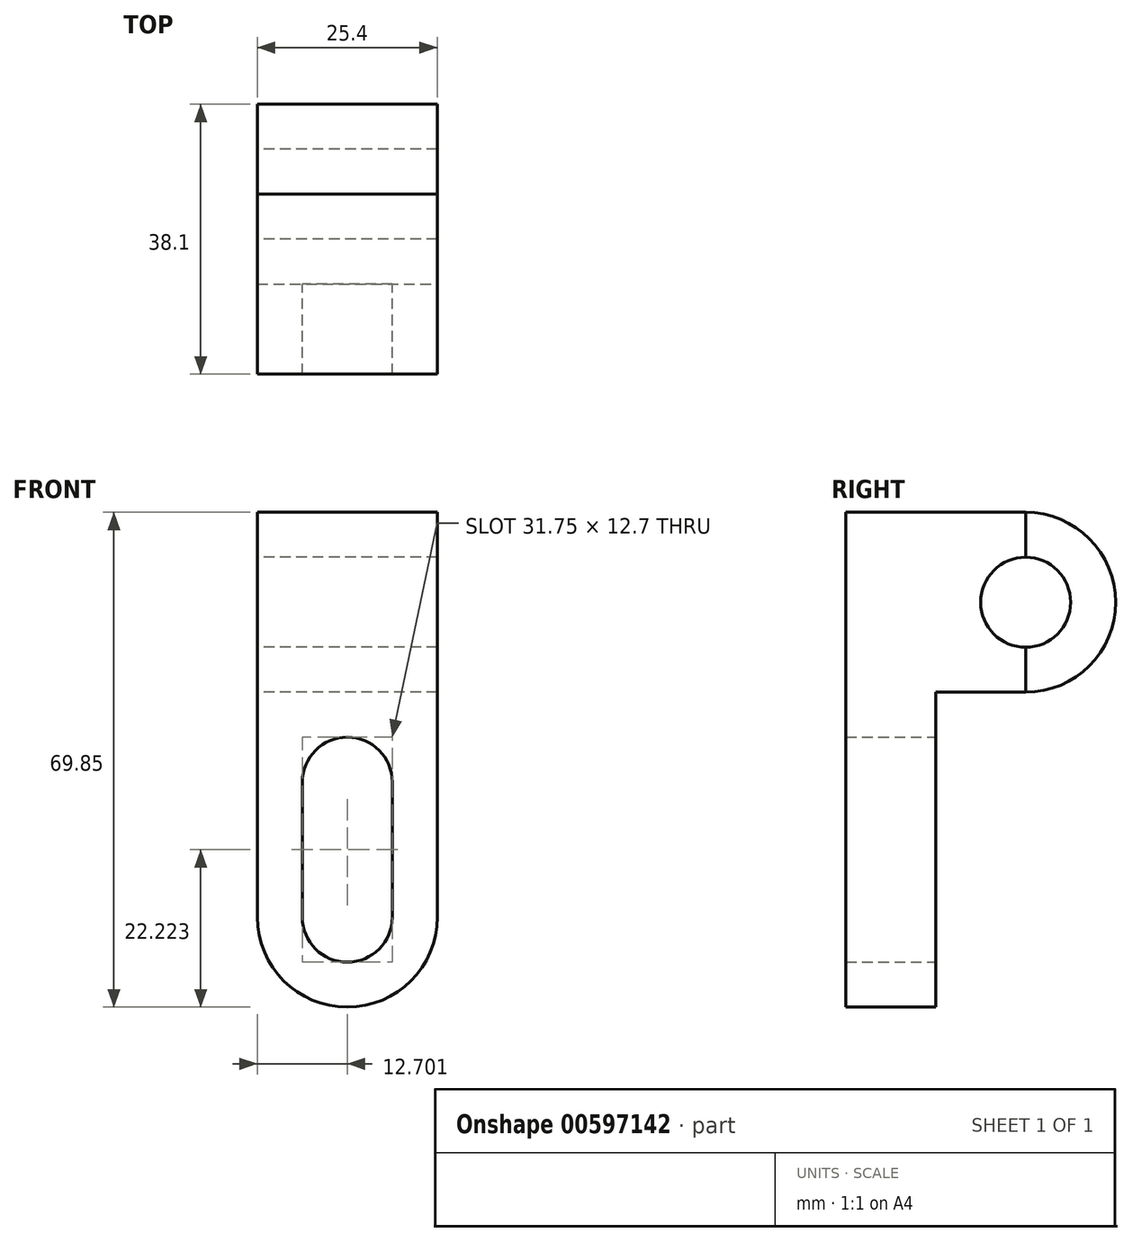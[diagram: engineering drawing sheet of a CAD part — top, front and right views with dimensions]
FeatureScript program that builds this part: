
annotation { "Feature Type Name" : "Feature", "Feature Type Description" : "" }
export const myFeature = defineFeature(function(context is Context, id is Id, definition is map)
    precondition{}
    {
        {
            var Q0;
            Q0=qCreatedBy(makeId("Front.planeOp"),FACE);
            var sketch = newSketch(context, id + "F0", { "sketchPlane" : qUnion([Q0])});
            skLineSegment(sketch, "E0", {"start": v(-59.54, 62.27) * mm, "end": v(-59.54, 5.12) * mm});
            skLineSegment(sketch, "E1", {"start": v(-59.54, 5.12) * mm, "end": v(-34.14, 5.12) * mm});
            skLineSegment(sketch, "E2", {"start": v(-34.14, 5.12) * mm, "end": v(-34.14, 62.27) * mm});
            skLineSegment(sketch, "E3", {"start": v(-34.14, 62.27) * mm, "end": v(-59.54, 62.27) * mm});
            skSolve(sketch);
        }
        {
            var Q0;
            Q0=makeQuery(id+"F0.imprint","IMPRINT",FACE,{"disambiguationData":[TD([[makeQuery(id+"F0.imprint","IMPRINT",EDGE,{"derivedFrom":sQuery(id+"F0.wireOp",EDGE,"E0")}),1.0]])]});
            extrude(context, id + "F1", {"entities" : qUnion([Q0]), "depth" : 12.7 * mm, "offsetDistance" : 25.4 * mm});
        }
        {
            var Q0;
            Q0=makeQuery(id+"F1.opExtrude","CAP_FACE",FACE,{"disambiguationData":[OSD([sQuery(id+"F0.wireOp",EDGE,"E0"),sQuery(id+"F0.wireOp",EDGE,"E1"),sQuery(id+"F0.wireOp",EDGE,"E2"),sQuery(id+"F0.wireOp",EDGE,"E3")])],"isStart":false});
            var sketch = newSketch(context, id + "F2", { "sketchPlane" : qUnion([Q0])});
            skArc(sketch, "E4", {"start": v(-59.54, 5.12) * mm, "mid": v(-46.84, -7.58) * mm, "end": v(-34.14, 5.12) * mm});
            skSolve(sketch);
        }
        {
            var Q0;
            Q0=makeQuery(id+"F2.imprint","IMPRINT",FACE,{"disambiguationData":[TD([[makeQuery(id+"F2.imprint","IMPRINT",EDGE,{"derivedFrom":sQuery(id+"F2.wireOp",EDGE,"E4")}),1.0]])]});
            var sketch = newSketch(context, id + "F3", { "sketchPlane" : qUnion([Q0])});
            skSolve(sketch);
        }
        {
            var Q0;
            Q0 = qSketchRegion(id + "F3", true);
            var Q1;
            Q1=makeQuery(id+"F2.imprint","IMPRINT",FACE,{"disambiguationData":[TD([[makeQuery(id+"F2.imprint","IMPRINT",EDGE,{"derivedFrom":sQuery(id+"F2.wireOp",EDGE,"E4")}),1.0]])]});
            extrude(context, id + "F4", {"entities" : qUnion([Q0, Q1]), "operationType" : NewBodyOperationType.ADD, "oppositeDirection" : true, "depth" : 12.7 * mm, "offsetDistance" : 25.4 * mm});
        }
        {
            var Q0;
            {var subQ0=sQuery(id+"F0.wireOp",EDGE,"E1");Q0=makeQuery(id+"F4.boolean.opBoolean","MERGE",FACE,{"derivedFrom":[makeQuery(id+"F1.opExtrude","CAP_FACE",FACE,{"disambiguationData":[OSD([sQuery(id+"F0.wireOp",EDGE,"E0"),subQ0,sQuery(id+"F0.wireOp",EDGE,"E2"),sQuery(id+"F0.wireOp",EDGE,"E3")])],"isStart":true}),makeQuery(id+"F4.opExtrude","CAP_FACE",FACE,{"disambiguationData":[OSD([subQ0,sQuery(id+"F2.wireOp",EDGE,"E4")])],"isStart":false})]});}
            var sketch = newSketch(context, id + "F5", { "sketchPlane" : qUnion([Q0])});
            skLineSegment(sketch, "E5", {"start": v(34.14, 62.27) * mm, "end": v(34.14, 36.87) * mm});
            skLineSegment(sketch, "E6", {"start": v(34.14, 36.87) * mm, "end": v(59.54, 36.87) * mm});
            skLineSegment(sketch, "E7", {"start": v(59.54, 36.87) * mm, "end": v(59.54, 62.27) * mm});
            skLineSegment(sketch, "E8", {"start": v(59.54, 62.27) * mm, "end": v(34.14, 62.27) * mm});
            skLineSegment(sketch, "E9", {"start": v(40.49, 24.17) * mm, "end": v(40.49, 5.12) * mm});
            skLineSegment(sketch, "E10", {"start": v(40.49, 5.12) * mm, "end": v(53.19, 5.12) * mm});
            skLineSegment(sketch, "E11", {"start": v(53.19, 5.12) * mm, "end": v(53.19, 24.17) * mm});
            skLineSegment(sketch, "E12", {"start": v(53.19, 24.17) * mm, "end": v(40.49, 24.17) * mm});
            skSolve(sketch);
        }
        {
            var Q0;
            Q0=makeQuery(id+"F5.imprint","IMPRINT",FACE,{"disambiguationData":[TD([[makeQuery(id+"F5.imprint","IMPRINT",EDGE,{"derivedFrom":sQuery(id+"F5.wireOp",EDGE,"E9")}),1.0]])]});
            extrude(context, id + "F6", {"entities" : qUnion([Q0]), "operationType" : NewBodyOperationType.REMOVE, "oppositeDirection" : true, "depth" : 25.4 * mm, "offsetDistance" : 25.4 * mm});
        }
        {
            var Q0;
            {var subQ0=sQuery(id+"F0.wireOp",EDGE,"E1");Q0=makeQuery(id+"F4.boolean.opBoolean","MERGE",FACE,{"derivedFrom":[makeQuery(id+"F1.opExtrude","CAP_FACE",FACE,{"disambiguationData":[OSD([sQuery(id+"F0.wireOp",EDGE,"E0"),subQ0,sQuery(id+"F0.wireOp",EDGE,"E2"),sQuery(id+"F0.wireOp",EDGE,"E3")])],"isStart":true}),makeQuery(id+"F4.opExtrude","CAP_FACE",FACE,{"disambiguationData":[OSD([subQ0,sQuery(id+"F2.wireOp",EDGE,"E4")])],"isStart":false})]});}
            var sketch = newSketch(context, id + "F7", { "sketchPlane" : qUnion([Q0])});
            skArc(sketch, "E13", {"start": v(53.19, 24.17) * mm, "mid": v(46.84, 30.52) * mm, "end": v(40.49, 24.17) * mm});
            skArc(sketch, "E14", {"start": v(40.49, 5.12) * mm, "mid": v(46.84, -1.23) * mm, "end": v(53.19, 5.12) * mm});
            skSolve(sketch);
        }
        {
            var Q0;
            Q0 = qSketchRegion(id + "F7", true);
            var Q1;
            Q1=makeQuery(id+"F7.imprint","IMPRINT",FACE,{"disambiguationData":[TD([[makeQuery(id+"F7.imprint","IMPRINT",EDGE,{"derivedFrom":sQuery(id+"F7.wireOp",EDGE,"E13")}),1.0]])]});
            extrude(context, id + "F8", {"entities" : qUnion([Q0, Q1]), "operationType" : NewBodyOperationType.REMOVE, "oppositeDirection" : true, "depth" : 25.4 * mm, "offsetDistance" : 25.4 * mm});
        }
        {
            var Q0;
            {var subQ0=sQuery(id+"F0.wireOp",EDGE,"E1");Q0=makeQuery(id+"F4.boolean.opBoolean","MERGE",FACE,{"derivedFrom":[makeQuery(id+"F1.opExtrude","CAP_FACE",FACE,{"disambiguationData":[OSD([sQuery(id+"F0.wireOp",EDGE,"E0"),subQ0,sQuery(id+"F0.wireOp",EDGE,"E2"),sQuery(id+"F0.wireOp",EDGE,"E3")])],"isStart":true}),makeQuery(id+"F4.opExtrude","CAP_FACE",FACE,{"disambiguationData":[OSD([subQ0,sQuery(id+"F2.wireOp",EDGE,"E4")])],"isStart":false})]});}
            var sketch = newSketch(context, id + "F9", { "sketchPlane" : qUnion([Q0])});
            skArc(sketch, "E15", {"start": v(40.49, 5.12) * mm, "mid": v(46.84, -1.23) * mm, "end": v(53.19, 5.12) * mm});
            skSolve(sketch);
        }
        {
            var Q0;
            Q0 = qSketchRegion(id + "F9", true);
            var Q1;
            Q1=makeQuery(id+"F9.imprint","IMPRINT",FACE,{"disambiguationData":[TD([[makeQuery(id+"F9.imprint","IMPRINT",EDGE,{"derivedFrom":sQuery(id+"F9.wireOp",EDGE,"E15")}),1.0]])]});
            extrude(context, id + "F10", {"entities" : qUnion([Q0, Q1]), "operationType" : NewBodyOperationType.REMOVE, "oppositeDirection" : true, "depth" : 25.4 * mm, "offsetDistance" : 25.4 * mm});
        }
        {
            var Q0;
            {var subQ0=sQuery(id+"F0.wireOp",EDGE,"E1");Q0=makeQuery(id+"F4.boolean.opBoolean","MERGE",FACE,{"derivedFrom":[makeQuery(id+"F1.opExtrude","CAP_FACE",FACE,{"disambiguationData":[OSD([sQuery(id+"F0.wireOp",EDGE,"E0"),subQ0,sQuery(id+"F0.wireOp",EDGE,"E2"),sQuery(id+"F0.wireOp",EDGE,"E3")])],"isStart":true}),makeQuery(id+"F4.opExtrude","CAP_FACE",FACE,{"disambiguationData":[OSD([subQ0,sQuery(id+"F2.wireOp",EDGE,"E4")])],"isStart":false})]});}
            var sketch = newSketch(context, id + "F11", { "sketchPlane" : qUnion([Q0])});
            skLineSegment(sketch, "E16", {"start": v(34.14, 62.27) * mm, "end": v(34.14, 36.87) * mm});
            skLineSegment(sketch, "E17", {"start": v(34.14, 36.87) * mm, "end": v(59.54, 36.87) * mm});
            skLineSegment(sketch, "E18", {"start": v(59.54, 36.87) * mm, "end": v(59.54, 62.27) * mm});
            skLineSegment(sketch, "E19", {"start": v(59.54, 62.27) * mm, "end": v(34.14, 62.27) * mm});
            skSolve(sketch);
        }
        {
            var Q0;
            Q0=makeQuery(id+"F11.imprint","IMPRINT",FACE,{"disambiguationData":[TD([[makeQuery(id+"F11.imprint","IMPRINT",EDGE,{"derivedFrom":sQuery(id+"F11.wireOp",EDGE,"E16")}),-1.0]])]});
            extrude(context, id + "F12", {"entities" : qUnion([Q0]), "operationType" : NewBodyOperationType.ADD, "depth" : 25.4 * mm, "offsetDistance" : 25.4 * mm});
        }
        {
            var Q0;
            Q0=makeQuery(id+"F12.opExtrude","CAP_FACE",FACE,{"disambiguationData":[OSD([sQuery(id+"F11.wireOp",EDGE,"E16"),sQuery(id+"F11.wireOp",EDGE,"E17"),sQuery(id+"F11.wireOp",EDGE,"E18"),sQuery(id+"F11.wireOp",EDGE,"E19")])],"isStart":false});
            var sketch = newSketch(context, id + "F13", { "sketchPlane" : qUnion([Q0])});
            skSolve(sketch);
        }
        {
            var Q0;
            Q0 = qSketchRegion(id + "F13", true);
            var Q1;
            Q1=makeQuery(id+"F13.imprint","IMPRINT",FACE,{"disambiguationData":[TD([[makeQuery(id+"F13.imprint","IMPRINT",EDGE,{"derivedFrom":makeQuery(id+"F12.opExtrude","CAP_EDGE",EDGE,{"disambiguationData":[OSD([sQuery(id+"F11.wireOp",EDGE,"E16")])],"isStart":false})}),-1.0]])]});
            extrude(context, id + "F14", {"entities" : qUnion([Q0, Q1]), "operationType" : NewBodyOperationType.REMOVE, "oppositeDirection" : true, "depth" : 25.4 * mm, "offsetDistance" : 25.4 * mm});
        }
        {
            var Q0;
            {var subQ0=sQuery(id+"F0.wireOp",EDGE,"E1");Q0=makeQuery(id+"F14.boolean.opBoolean","MERGE",FACE,{"derivedFrom":[makeQuery(id+"F4.boolean.opBoolean","MERGE",FACE,{"derivedFrom":[makeQuery(id+"F1.opExtrude","CAP_FACE",FACE,{"disambiguationData":[OSD([sQuery(id+"F0.wireOp",EDGE,"E0"),subQ0,sQuery(id+"F0.wireOp",EDGE,"E2"),sQuery(id+"F0.wireOp",EDGE,"E3")])],"isStart":true}),makeQuery(id+"F4.opExtrude","CAP_FACE",FACE,{"disambiguationData":[OSD([subQ0,sQuery(id+"F2.wireOp",EDGE,"E4")])],"isStart":false})]}),makeQuery(id+"F14.opExtrude","CAP_FACE",FACE,{"disambiguationData":[OSD([sQuery(id+"F11.wireOp",EDGE,"E16"),sQuery(id+"F11.wireOp",EDGE,"E17"),sQuery(id+"F11.wireOp",EDGE,"E18"),sQuery(id+"F11.wireOp",EDGE,"E19")])],"isStart":false})]});}
            var sketch = newSketch(context, id + "F15", { "sketchPlane" : qUnion([Q0])});
            skLineSegment(sketch, "E20", {"start": v(34.14, 62.27) * mm, "end": v(59.54, 62.27) * mm});
            skLineSegment(sketch, "E21", {"start": v(59.54, 62.27) * mm, "end": v(59.54, 36.87) * mm});
            skLineSegment(sketch, "E22", {"start": v(59.54, 36.87) * mm, "end": v(34.14, 36.87) * mm});
            skLineSegment(sketch, "E23", {"start": v(34.14, 36.87) * mm, "end": v(34.14, 62.27) * mm});
            skSolve(sketch);
        }
        {
            var Q0;
            Q0=makeQuery(id+"F15.imprint","IMPRINT",FACE,{"disambiguationData":[TD([[makeQuery(id+"F15.imprint","IMPRINT",EDGE,{"derivedFrom":sQuery(id+"F15.wireOp",EDGE,"E20")}),-1.0]])]});
            extrude(context, id + "F16", {"entities" : qUnion([Q0]), "operationType" : NewBodyOperationType.ADD, "depth" : 12.7 * mm, "offsetDistance" : 25.4 * mm});
        }
        {
            var Q0;
            Q0=makeQuery(id+"F16.boolean.opBoolean","MERGE",FACE,{"derivedFrom":[makeQuery(id+"F12.boolean.opBoolean","MERGE",FACE,{"derivedFrom":[makeQuery(id+"F1.opExtrude","SWEPT_FACE",FACE,{"disambiguationData":[OSD([sQuery(id+"F0.wireOp",EDGE,"E0")])]}),makeQuery(id+"F12.opExtrude","SWEPT_FACE",FACE,{"disambiguationData":[OSD([sQuery(id+"F11.wireOp",EDGE,"E18")])]})]}),makeQuery(id+"F16.opExtrude","SWEPT_FACE",FACE,{"disambiguationData":[OSD([sQuery(id+"F15.wireOp",EDGE,"E21")])]})]});
            var sketch = newSketch(context, id + "F17", { "sketchPlane" : qUnion([Q0])});
            skArc(sketch, "E24", {"start": v(-12.7, 62.27) * mm, "mid": v(-25.4, 49.57) * mm, "end": v(-12.7, 36.87) * mm});
            skSolve(sketch);
        }
        {
            var Q0;
            Q0 = qSketchRegion(id + "F17", true);
            var Q1;
            Q1=makeQuery(id+"F17.imprint","IMPRINT",FACE,{"disambiguationData":[TD([[makeQuery(id+"F17.imprint","IMPRINT",EDGE,{"derivedFrom":sQuery(id+"F17.wireOp",EDGE,"E24")}),1.0]])]});
            extrude(context, id + "F18", {"entities" : qUnion([Q0, Q1]), "oppositeDirection" : true, "depth" : 25.4 * mm, "offsetDistance" : 25.4 * mm});
        }
        {
            var Q0;
            Q0=makeQuery(id+"F18.opExtrude","CAP_FACE",FACE,{"disambiguationData":[OSD([sQuery(id+"F15.wireOp",EDGE,"E21"),sQuery(id+"F17.wireOp",EDGE,"E24")])],"isStart":true});
            var sketch = newSketch(context, id + "F19", { "sketchPlane" : qUnion([Q0])});
            skCircle(sketch, "E25", {"center": v(-12.7, 49.57) * mm, "radius": 6.35 * mm});
            skSolve(sketch);
        }
        {
            var Q0;
            {var subQ0=sQuery(id+"F19.wireOp",EDGE,"E25");var subQ1=makeQuery(id+"F18.opExtrude","CAP_EDGE",EDGE,{"disambiguationData":[OSD([sQuery(id+"F15.wireOp",EDGE,"E21")])],"isStart":true});var subQ2=makeQuery(id+"F19.imprint","INTERSECT",VERTEX,{"disambiguationData":[OD(0.0)],"derivedFrom":[subQ1,subQ0]});Q0=makeQuery(id+"F19.imprint","IMPRINT",FACE,{"disambiguationData":[TD([[makeQuery(id+"F19.imprint","IMPRINT",EDGE,{"disambiguationData":[TD([[subQ2,1.0]])],"derivedFrom":subQ0}),1.0]])]});}
            var sketch = newSketch(context, id + "F20", { "sketchPlane" : qUnion([Q0])});
            skSolve(sketch);
        }
        {
            var Q0;
            {var subQ0=sQuery(id+"F19.wireOp",EDGE,"E25");var subQ1=makeQuery(id+"F18.opExtrude","CAP_EDGE",EDGE,{"disambiguationData":[OSD([sQuery(id+"F15.wireOp",EDGE,"E21")])],"isStart":true});var subQ2=makeQuery(id+"F19.imprint","INTERSECT",VERTEX,{"disambiguationData":[OD(0.0)],"derivedFrom":[subQ1,subQ0]});Q0=makeQuery(id+"F19.imprint","IMPRINT",FACE,{"disambiguationData":[TD([[makeQuery(id+"F19.imprint","IMPRINT",EDGE,{"disambiguationData":[TD([[subQ2,-1.0]])],"derivedFrom":subQ0}),1.0]])]});}
            var sketch = newSketch(context, id + "F21", { "sketchPlane" : qUnion([Q0])});
            skSolve(sketch);
        }
        {
            var Q0;
            {var subQ0=sQuery(id+"F19.wireOp",EDGE,"E25");var subQ1=makeQuery(id+"F18.opExtrude","CAP_EDGE",EDGE,{"disambiguationData":[OSD([sQuery(id+"F15.wireOp",EDGE,"E21")])],"isStart":true});var subQ2=makeQuery(id+"F19.imprint","INTERSECT",VERTEX,{"disambiguationData":[OD(0.0)],"derivedFrom":[subQ1,subQ0]});Q0=makeQuery(id+"F19.imprint","IMPRINT",FACE,{"disambiguationData":[TD([[makeQuery(id+"F19.imprint","IMPRINT",EDGE,{"disambiguationData":[TD([[subQ2,1.0]])],"derivedFrom":subQ0}),1.0]])]});}
            var Q1;
            {var subQ0=sQuery(id+"F19.wireOp",EDGE,"E25");var subQ1=makeQuery(id+"F18.opExtrude","CAP_EDGE",EDGE,{"disambiguationData":[OSD([sQuery(id+"F15.wireOp",EDGE,"E21")])],"isStart":true});var subQ2=makeQuery(id+"F19.imprint","INTERSECT",VERTEX,{"disambiguationData":[OD(0.0)],"derivedFrom":[subQ1,subQ0]});Q1=makeQuery(id+"F19.imprint","IMPRINT",FACE,{"disambiguationData":[TD([[makeQuery(id+"F19.imprint","IMPRINT",EDGE,{"disambiguationData":[TD([[subQ2,-1.0]])],"derivedFrom":subQ0}),1.0]])]});}
            extrude(context, id + "F22", {"entities" : qUnion([Q0, Q1]), "operationType" : NewBodyOperationType.REMOVE, "oppositeDirection" : true, "depth" : 25.4 * mm, "offsetDistance" : 25.4 * mm});
        }
        {
            var Q0;
            {var subQ0=sQuery(id+"F19.wireOp",EDGE,"E25");var subQ1=makeQuery(id+"F18.opExtrude","CAP_EDGE",EDGE,{"disambiguationData":[OSD([sQuery(id+"F15.wireOp",EDGE,"E21")])],"isStart":true});var subQ2=makeQuery(id+"F19.imprint","INTERSECT",VERTEX,{"disambiguationData":[OD(0.0)],"derivedFrom":[subQ1,subQ0]});Q0=makeQuery(id+"F20.imprint","IMPRINT",FACE,{"disambiguationData":[TD([[makeQuery(id+"F20.imprint","IMPRINT",EDGE,{"derivedFrom":makeQuery(id+"F19.imprint","IMPRINT",EDGE,{"disambiguationData":[TD([[subQ2,1.0]])],"derivedFrom":subQ0})}),1.0]])]});}
            var Q1;
            {var subQ0=sQuery(id+"F19.wireOp",EDGE,"E25");var subQ1=makeQuery(id+"F18.opExtrude","CAP_EDGE",EDGE,{"disambiguationData":[OSD([sQuery(id+"F15.wireOp",EDGE,"E21")])],"isStart":true});var subQ2=makeQuery(id+"F19.imprint","INTERSECT",VERTEX,{"disambiguationData":[OD(0.0)],"derivedFrom":[subQ1,subQ0]});Q1=makeQuery(id+"F21.imprint","IMPRINT",FACE,{"disambiguationData":[TD([[makeQuery(id+"F21.imprint","IMPRINT",EDGE,{"derivedFrom":makeQuery(id+"F19.imprint","IMPRINT",EDGE,{"disambiguationData":[TD([[subQ2,-1.0]])],"derivedFrom":subQ0})}),1.0]])]});}
            extrude(context, id + "F23", {"entities" : qUnion([Q0, Q1]), "operationType" : NewBodyOperationType.REMOVE, "oppositeDirection" : true, "depth" : 25.4 * mm, "offsetDistance" : 25.4 * mm});
        }
        {
            var Q0;
            Q0=makeQuery(id+"F16.boolean.opBoolean","MERGE",FACE,{"derivedFrom":[makeQuery(id+"F12.boolean.opBoolean","MERGE",FACE,{"derivedFrom":[makeQuery(id+"F1.opExtrude","SWEPT_FACE",FACE,{"disambiguationData":[OSD([sQuery(id+"F0.wireOp",EDGE,"E0")])]}),makeQuery(id+"F12.opExtrude","SWEPT_FACE",FACE,{"disambiguationData":[OSD([sQuery(id+"F11.wireOp",EDGE,"E18")])]})]}),makeQuery(id+"F16.opExtrude","SWEPT_FACE",FACE,{"disambiguationData":[OSD([sQuery(id+"F15.wireOp",EDGE,"E21")])]})]});
            var sketch = newSketch(context, id + "F24", { "sketchPlane" : qUnion([Q0])});
            skCircle(sketch, "E26", {"center": v(-12.7, 49.57) * mm, "radius": 6.35 * mm});
            skSolve(sketch);
        }
        {
            var Q0;
            {var subQ0=sQuery(id+"F24.wireOp",EDGE,"E26");var subQ1=makeQuery(id+"F16.opExtrude","CAP_EDGE",EDGE,{"disambiguationData":[OSD([sQuery(id+"F15.wireOp",EDGE,"E21")])],"isStart":false});var subQ2=makeQuery(id+"F24.imprint","INTERSECT",VERTEX,{"disambiguationData":[OD(0.0)],"derivedFrom":[subQ1,subQ0]});Q0=makeQuery(id+"F24.imprint","IMPRINT",FACE,{"disambiguationData":[TD([[makeQuery(id+"F24.imprint","IMPRINT",EDGE,{"disambiguationData":[TD([[subQ2,-1.0]])],"derivedFrom":subQ0}),1.0]])]});}
            var Q1;
            {var subQ0=sQuery(id+"F24.wireOp",EDGE,"E26");var subQ1=makeQuery(id+"F16.opExtrude","CAP_EDGE",EDGE,{"disambiguationData":[OSD([sQuery(id+"F15.wireOp",EDGE,"E21")])],"isStart":false});var subQ2=makeQuery(id+"F24.imprint","INTERSECT",VERTEX,{"disambiguationData":[OD(0.0)],"derivedFrom":[subQ1,subQ0]});Q1=makeQuery(id+"F24.imprint","IMPRINT",FACE,{"disambiguationData":[TD([[makeQuery(id+"F24.imprint","IMPRINT",EDGE,{"disambiguationData":[TD([[subQ2,1.0]])],"derivedFrom":subQ0}),1.0]])]});}
            extrude(context, id + "F25", {"entities" : qUnion([Q0, Q1]), "operationType" : NewBodyOperationType.REMOVE, "oppositeDirection" : true, "depth" : 25.4 * mm, "offsetDistance" : 25.4 * mm});
        }
        {
            var Q0;
            Q0=makeQuery(id+"F16.boolean.opBoolean","MERGE",FACE,{"derivedFrom":[makeQuery(id+"F12.boolean.opBoolean","MERGE",FACE,{"derivedFrom":[makeQuery(id+"F1.opExtrude","SWEPT_FACE",FACE,{"disambiguationData":[OSD([sQuery(id+"F0.wireOp",EDGE,"E0")])]}),makeQuery(id+"F12.opExtrude","SWEPT_FACE",FACE,{"disambiguationData":[OSD([sQuery(id+"F11.wireOp",EDGE,"E18")])]})]}),makeQuery(id+"F16.opExtrude","SWEPT_FACE",FACE,{"disambiguationData":[OSD([sQuery(id+"F15.wireOp",EDGE,"E21")])]})]});
            var sketch = newSketch(context, id + "F26", { "sketchPlane" : qUnion([Q0])});
            skCircle(sketch, "E27", {"center": v(-12.7, 49.57) * mm, "radius": 6.35 * mm});
            skSolve(sketch);
        }
        {
            var Q0;
            {var subQ0=sQuery(id+"F26.wireOp",EDGE,"E27");var subQ1=makeQuery(id+"F16.opExtrude","CAP_EDGE",EDGE,{"disambiguationData":[OSD([sQuery(id+"F15.wireOp",EDGE,"E21")])],"isStart":false});var subQ2=makeQuery(id+"F26.imprint","INTERSECT",VERTEX,{"disambiguationData":[OD(0.0)],"derivedFrom":[subQ1,subQ0]});Q0=makeQuery(id+"F26.imprint","IMPRINT",FACE,{"disambiguationData":[TD([[makeQuery(id+"F26.imprint","IMPRINT",EDGE,{"disambiguationData":[TD([[subQ2,-1.0]])],"derivedFrom":subQ0}),1.0]])]});}
            var Q1;
            {var subQ0=sQuery(id+"F26.wireOp",EDGE,"E27");var subQ1=makeQuery(id+"F16.opExtrude","CAP_EDGE",EDGE,{"disambiguationData":[OSD([sQuery(id+"F15.wireOp",EDGE,"E21")])],"isStart":false});var subQ2=makeQuery(id+"F26.imprint","INTERSECT",VERTEX,{"disambiguationData":[OD(0.0)],"derivedFrom":[subQ1,subQ0]});Q1=makeQuery(id+"F26.imprint","IMPRINT",FACE,{"disambiguationData":[TD([[makeQuery(id+"F26.imprint","IMPRINT",EDGE,{"disambiguationData":[TD([[subQ2,1.0]])],"derivedFrom":subQ0}),1.0]])]});}
            extrude(context, id + "F27", {"entities" : qUnion([Q0, Q1]), "operationType" : NewBodyOperationType.REMOVE, "oppositeDirection" : true, "depth" : 25.4 * mm, "offsetDistance" : 25.4 * mm});
        }
    });
